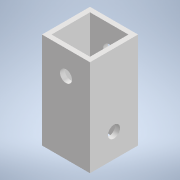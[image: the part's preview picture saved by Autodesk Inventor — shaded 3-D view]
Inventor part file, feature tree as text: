
AUTODESK INVENTOR PART (.ipt)
format: ipt  version: 2020.3 (Build 243373000, 373)  size: 119,296 bytes
history: native  units: mm
features: sketch x3, hole x2, other x1, extrude x1
ambient origin geometry x8: Origin, YZ Plane, XZ Plane, XY Plane, X Axis, Y Axis, Z Axis, Center Point
bodies: Body1 (feature_tree)
feature tree (7):
  other  "ソリッド1"
  extrude  "押し出し1"  Depth=12.0mm
  hole  "穴1"  [1 undecoded]
  hole  "穴2"  [1 undecoded]
  sketch  "スケッチ1"
  sketch  "スケッチ2"
  sketch  "スケッチ3"
note: 2 required parameter values undecoded (feature->parameter linkage not recoverable at this tier; creation-order binding heuristic only, values carry confidence <= 0.55)
